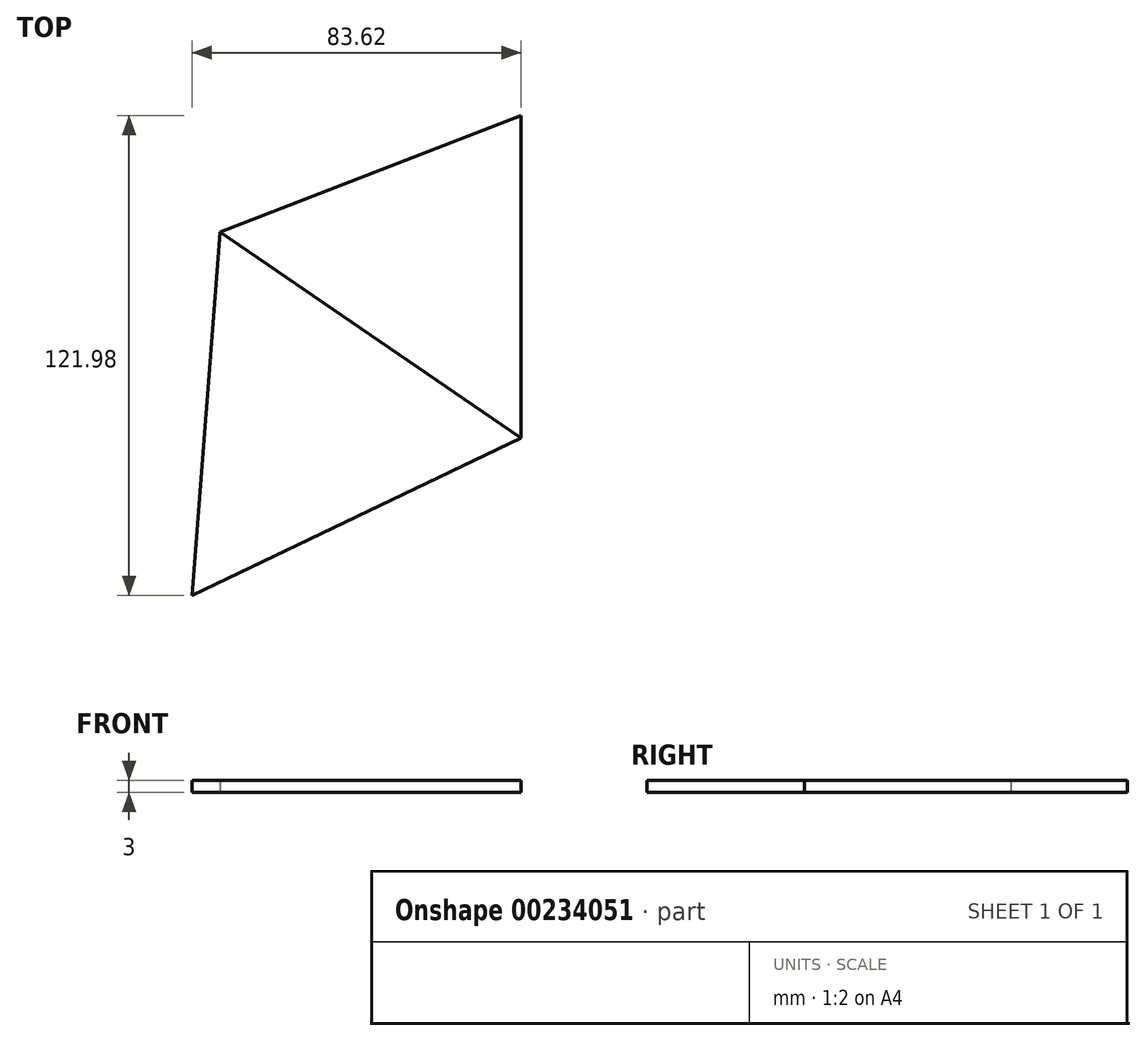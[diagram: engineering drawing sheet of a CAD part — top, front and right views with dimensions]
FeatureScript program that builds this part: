
annotation { "Feature Type Name" : "Feature", "Feature Type Description" : "" }
export const myFeature = defineFeature(function(context is Context, id is Id, definition is map)
    precondition{}
    {
        {
            var Q0;
            Q0=qCreatedBy(makeId("Top.planeOp"),FACE);
            var sketch = newSketch(context, id + "F0", { "sketchPlane" : qUnion([Q0])});
            skLineSegment(sketch, "E0", {"start": v(0, 0) * mm, "end": v(0, -81.97) * mm});
            skLineSegment(sketch, "E1", {"start": v(0, -81.97) * mm, "end": v(-76.46, -29.56) * mm});
            skLineSegment(sketch, "E2", {"start": v(-76.46, -29.56) * mm, "end": v(0, 0) * mm});
            skLineSegment(sketch, "E3", {"start": v(-76.46, -29.56) * mm, "end": v(-83.62, -121.98) * mm});
            skLineSegment(sketch, "E4", {"start": v(-83.62, -121.98) * mm, "end": v(0, -81.97) * mm});
            skLineSegment(sketch, "E5", {"start": v(-76.46, -29.56) * mm, "end": v(-147.45, -70.55) * mm});
            skLineSegment(sketch, "E6", {"start": v(-147.45, -70.55) * mm, "end": v(-83.62, -121.98) * mm});
            skLineSegment(sketch, "E7", {"start": v(-83.62, -121.98) * mm, "end": v(-12.63, -162.97) * mm});
            skLineSegment(sketch, "E8", {"start": v(-12.63, -162.97) * mm, "end": v(0, -81.97) * mm});
            skLineSegment(sketch, "E9", {"start": v(-83.62, -121.98) * mm, "end": v(-172.4, -148.63) * mm});
            skLineSegment(sketch, "E10", {"start": v(-172.4, -148.63) * mm, "end": v(-104.94, -212.2) * mm});
            skLineSegment(sketch, "E11", {"start": v(-104.94, -212.2) * mm, "end": v(-83.62, -121.98) * mm});
            skLineSegment(sketch, "E12", {"start": v(-172.4, -148.63) * mm, "end": v(-147.45, -70.55) * mm});
            skLineSegment(sketch, "E13", {"start": v(-83.62, -121.98) * mm, "end": v(-28.48, -182.64) * mm});
            skLineSegment(sketch, "E14", {"start": v(-28.48, -182.64) * mm, "end": v(-104.94, -212.2) * mm});
            skLineSegment(sketch, "E15", {"start": v(-104.94, -212.2) * mm, "end": v(-28.48, -264.61) * mm});
            skLineSegment(sketch, "E16", {"start": v(-28.48, -264.61) * mm, "end": v(-28.48, -182.64) * mm});
            skLineSegment(sketch, "E17.1.0", {"start": v(-257.08, -68.86) * mm, "end": v(-180.62, -39.3) * mm});
            skLineSegment(sketch, "E17.1.1", {"start": v(-180.62, -39.3) * mm, "end": v(-235.76, 21.36) * mm});
            skLineSegment(sketch, "E17.1.2", {"start": v(-235.76, 21.36) * mm, "end": v(-257.08, -68.86) * mm});
            skLineSegment(sketch, "E17.1.3", {"start": v(-76.46, -29.56) * mm, "end": v(-55.14, 60.66) * mm});
            skLineSegment(sketch, "E17.1.4", {"start": v(-55.14, 60.66) * mm, "end": v(-143.93, 34) * mm});
            skLineSegment(sketch, "E17.1.5", {"start": v(0, 0) * mm, "end": v(-76.46, -29.56) * mm});
            skLineSegment(sketch, "E17.1.6", {"start": v(-143.93, 34) * mm, "end": v(-76.46, -29.56) * mm});
            skLineSegment(sketch, "E17.1.7", {"start": v(-55.14, 60.66) * mm, "end": v(-118.97, 112.1) * mm});
            skLineSegment(sketch, "E17.1.8", {"start": v(-200.8, 107.21) * mm, "end": v(-118.97, 112.1) * mm});
            skLineSegment(sketch, "E17.1.9", {"start": v(-235.76, 21.36) * mm, "end": v(-143.93, 34) * mm});
            skLineSegment(sketch, "E17.1.10", {"start": v(-118.97, 112.1) * mm, "end": v(-143.93, 34) * mm});
            skLineSegment(sketch, "E17.1.11", {"start": v(-143.93, 34) * mm, "end": v(-180.62, -39.3) * mm});
            skLineSegment(sketch, "E17.1.12", {"start": v(-200.8, 107.21) * mm, "end": v(-235.76, 21.36) * mm});
            skLineSegment(sketch, "E17.1.13", {"start": v(-143.93, 34) * mm, "end": v(-156.56, -46.99) * mm});
            skLineSegment(sketch, "E17.1.14", {"start": v(-156.56, -46.99) * mm, "end": v(-76.46, -29.56) * mm});
            skLineSegment(sketch, "E17.1.15", {"start": v(-143.93, 34) * mm, "end": v(-200.8, 107.21) * mm});
            skLineSegment(sketch, "E17.2.0", {"start": v(-156.93, 214.95) * mm, "end": v(-101.79, 154.3) * mm});
            skLineSegment(sketch, "E17.2.1", {"start": v(-101.79, 154.3) * mm, "end": v(-65.1, 227.6) * mm});
            skLineSegment(sketch, "E17.2.2", {"start": v(-65.1, 227.6) * mm, "end": v(-156.93, 214.95) * mm});
            skLineSegment(sketch, "E17.2.3", {"start": v(-55.14, 60.66) * mm, "end": v(36.69, 73.3) * mm});
            skLineSegment(sketch, "E17.2.4", {"start": v(36.69, 73.3) * mm, "end": v(-20.18, 146.51) * mm});
            skLineSegment(sketch, "E17.2.5", {"start": v(0, 0) * mm, "end": v(-55.14, 60.66) * mm});
            skLineSegment(sketch, "E17.2.6", {"start": v(-20.18, 146.51) * mm, "end": v(-55.14, 60.66) * mm});
            skLineSegment(sketch, "E17.2.7", {"start": v(36.69, 73.3) * mm, "end": v(61.65, 151.4) * mm});
            skLineSegment(sketch, "E17.2.8", {"start": v(27.59, 225.95) * mm, "end": v(61.65, 151.4) * mm});
            skLineSegment(sketch, "E17.2.9", {"start": v(-65.1, 227.6) * mm, "end": v(-20.18, 146.51) * mm});
            skLineSegment(sketch, "E17.2.10", {"start": v(61.65, 151.4) * mm, "end": v(-20.18, 146.51) * mm});
            skLineSegment(sketch, "E17.2.11", {"start": v(-20.18, 146.51) * mm, "end": v(-101.79, 154.3) * mm});
            skLineSegment(sketch, "E17.2.12", {"start": v(27.59, 225.95) * mm, "end": v(-65.1, 227.6) * mm});
            skLineSegment(sketch, "E17.2.13", {"start": v(-20.18, 146.51) * mm, "end": v(-100.28, 129.08) * mm});
            skLineSegment(sketch, "E17.2.14", {"start": v(-100.28, 129.08) * mm, "end": v(-55.14, 60.66) * mm});
            skLineSegment(sketch, "E17.2.15", {"start": v(-20.18, 146.51) * mm, "end": v(27.59, 225.95) * mm});
            skLineSegment(sketch, "E17.3.0", {"start": v(143.9, 223.89) * mm, "end": v(107.2, 150.58) * mm});
            skLineSegment(sketch, "E17.3.1", {"start": v(107.2, 150.58) * mm, "end": v(188.81, 142.8) * mm});
            skLineSegment(sketch, "E17.3.2", {"start": v(188.81, 142.8) * mm, "end": v(143.9, 223.89) * mm});
            skLineSegment(sketch, "E17.3.3", {"start": v(36.69, 73.3) * mm, "end": v(81.6, -7.79) * mm});
            skLineSegment(sketch, "E17.3.4", {"start": v(81.6, -7.79) * mm, "end": v(129.37, 71.66) * mm});
            skLineSegment(sketch, "E17.3.5", {"start": v(0, 0) * mm, "end": v(36.69, 73.3) * mm});
            skLineSegment(sketch, "E17.3.6", {"start": v(129.37, 71.66) * mm, "end": v(36.69, 73.3) * mm});
            skLineSegment(sketch, "E17.3.7", {"start": v(81.6, -7.79) * mm, "end": v(163.43, -2.9) * mm});
            skLineSegment(sketch, "E17.3.8", {"start": v(220.7, 55.75) * mm, "end": v(163.43, -2.9) * mm});
            skLineSegment(sketch, "E17.3.9", {"start": v(188.81, 142.8) * mm, "end": v(129.37, 71.66) * mm});
            skLineSegment(sketch, "E17.3.10", {"start": v(163.43, -2.9) * mm, "end": v(129.37, 71.66) * mm});
            skLineSegment(sketch, "E17.3.11", {"start": v(129.37, 71.66) * mm, "end": v(107.2, 150.58) * mm});
            skLineSegment(sketch, "E17.3.12", {"start": v(220.7, 55.75) * mm, "end": v(188.81, 142.8) * mm});
            skLineSegment(sketch, "E17.3.13", {"start": v(129.37, 71.66) * mm, "end": v(84.23, 140.09) * mm});
            skLineSegment(sketch, "E17.3.14", {"start": v(84.23, 140.09) * mm, "end": v(36.69, 73.3) * mm});
            skLineSegment(sketch, "E17.3.15", {"start": v(129.37, 71.66) * mm, "end": v(220.7, 55.75) * mm});
            skLineSegment(sketch, "E17.4.0", {"start": v(260.71, -53.48) * mm, "end": v(179.1, -45.7) * mm});
            skLineSegment(sketch, "E17.4.1", {"start": v(179.1, -45.7) * mm, "end": v(201.27, -124.62) * mm});
            skLineSegment(sketch, "E17.4.2", {"start": v(201.27, -124.62) * mm, "end": v(260.71, -53.48) * mm});
            skLineSegment(sketch, "E17.4.3", {"start": v(81.6, -7.79) * mm, "end": v(22.17, -78.92) * mm});
            skLineSegment(sketch, "E17.4.4", {"start": v(22.17, -78.92) * mm, "end": v(113.5, -94.83) * mm});
            skLineSegment(sketch, "E17.4.5", {"start": v(0, 0) * mm, "end": v(81.6, -7.79) * mm});
            skLineSegment(sketch, "E17.4.6", {"start": v(113.5, -94.83) * mm, "end": v(81.6, -7.79) * mm});
            skLineSegment(sketch, "E17.4.7", {"start": v(22.17, -78.92) * mm, "end": v(56.23, -153.49) * mm});
            skLineSegment(sketch, "E17.4.8", {"start": v(131.59, -185.75) * mm, "end": v(56.23, -153.49) * mm});
            skLineSegment(sketch, "E17.4.9", {"start": v(201.27, -124.62) * mm, "end": v(113.5, -94.83) * mm});
            skLineSegment(sketch, "E17.4.10", {"start": v(56.23, -153.49) * mm, "end": v(113.5, -94.83) * mm});
            skLineSegment(sketch, "E17.4.11", {"start": v(113.5, -94.83) * mm, "end": v(179.1, -45.7) * mm});
            skLineSegment(sketch, "E17.4.12", {"start": v(131.59, -185.75) * mm, "end": v(201.27, -124.62) * mm});
            skLineSegment(sketch, "E17.4.13", {"start": v(113.5, -94.83) * mm, "end": v(161.04, -28.05) * mm});
            skLineSegment(sketch, "E17.4.14", {"start": v(161.04, -28.05) * mm, "end": v(81.6, -7.79) * mm});
            skLineSegment(sketch, "E17.4.15", {"start": v(113.5, -94.83) * mm, "end": v(131.59, -185.75) * mm});
            skPoint(sketch, "E17.center", {"position": v(0, 0) * mm});
            skLineSegment(sketch, "E17.anchor1", {"start": v(0, 0) * mm, "end": v(-172.4, -148.63) * mm, "construction": true});
            skLineSegment(sketch, "E17.anchor2", {"start": v(0, 0) * mm, "end": v(131.59, -185.75) * mm, "construction": true});
            skLineSegment(sketch, "E18", {"start": v(0, 0) * mm, "end": v(22.17, -78.92) * mm});
            skLineSegment(sketch, "E19.MirrorCS", {"start": v(-456.15, 107.78) * mm, "end": v(-401.01, 47.12) * mm});
            skLineSegment(sketch, "E20.MirrorCS", {"start": v(-379.7, 322.18) * mm, "end": v(-296.07, 282.17) * mm});
            skLineSegment(sketch, "E21.MirrorCS", {"start": v(-401.01, 47.12) * mm, "end": v(-456.15, 107.78) * mm});
            skLineSegment(sketch, "E22.MirrorCS", {"start": v(-456.15, 107.78) * mm, "end": v(-511.3, 47.12) * mm});
            skLineSegment(sketch, "E23.MirrorCS", {"start": v(-456.15, 107.78) * mm, "end": v(-492.84, 34.47) * mm});
            skLineSegment(sketch, "E24.MirrorCS", {"start": v(-492.84, 34.47) * mm, "end": v(-401.01, 47.12) * mm});
            skLineSegment(sketch, "E25.MirrorCS", {"start": v(-401.01, 47.12) * mm, "end": v(-355.87, -21.3) * mm});
            skLineSegment(sketch, "E26.MirrorCS", {"start": v(-401.01, 47.12) * mm, "end": v(-435.97, -38.73) * mm});
            skLineSegment(sketch, "E27.MirrorCS", {"start": v(-435.97, -38.73) * mm, "end": v(-492.84, 34.47) * mm});
            skLineSegment(sketch, "E28.MirrorCS", {"start": v(-435.97, -38.73) * mm, "end": v(-517.8, -43.61) * mm});
            skLineSegment(sketch, "E29.MirrorCS", {"start": v(-435.97, -38.73) * mm, "end": v(-368.5, -102.3) * mm});
            skLineSegment(sketch, "E30.MirrorCS", {"start": v(-435.97, -38.73) * mm, "end": v(-512.43, -68.3) * mm});
            skLineSegment(sketch, "E31.MirrorCS", {"start": v(-457.29, -128.95) * mm, "end": v(-435.97, -38.73) * mm});
            skLineSegment(sketch, "E32.MirrorCS", {"start": v(-512.43, -68.3) * mm, "end": v(-457.29, -128.95) * mm});
            skLineSegment(sketch, "E33.MirrorCS", {"start": v(-296.07, 282.17) * mm, "end": v(-219.61, 229.76) * mm});
            skLineSegment(sketch, "E34.MirrorCS", {"start": v(-561.1, 319.98) * mm, "end": v(-484.63, 372.4) * mm});
            skLineSegment(sketch, "E35.MirrorCS", {"start": v(-484.63, 372.4) * mm, "end": v(-484.63, 290.42) * mm});
            skLineSegment(sketch, "E36.MirrorCS", {"start": v(-379.7, 322.18) * mm, "end": v(-443.53, 270.75) * mm});
            skLineSegment(sketch, "E37.MirrorCS", {"start": v(-372.53, 229.76) * mm, "end": v(-379.7, 322.18) * mm});
            skLineSegment(sketch, "E38.MirrorCS", {"start": v(-296.07, 282.17) * mm, "end": v(-372.53, 229.76) * mm});
            skLineSegment(sketch, "E39.MirrorCS", {"start": v(-296.07, 200.2) * mm, "end": v(-296.07, 282.17) * mm});
            skLineSegment(sketch, "E40.MirrorCS", {"start": v(-219.61, 229.76) * mm, "end": v(-296.07, 200.2) * mm});
            skLineSegment(sketch, "E41.MirrorCS", {"start": v(-484.63, 290.42) * mm, "end": v(-561.1, 319.98) * mm});
            skLineSegment(sketch, "E42.MirrorCS", {"start": v(-443.53, 270.75) * mm, "end": v(-372.53, 229.76) * mm});
            skLineSegment(sketch, "E43.MirrorCS", {"start": v(-372.53, 229.76) * mm, "end": v(-296.07, 200.2) * mm});
            skLineSegment(sketch, "E44.MirrorCS", {"start": v(-372.53, 229.76) * mm, "end": v(-308.7, 178.33) * mm});
            skLineSegment(sketch, "E45.MirrorCS", {"start": v(-561.1, 319.98) * mm, "end": v(-539.78, 229.76) * mm});
            skLineSegment(sketch, "E46.MirrorCS", {"start": v(-539.78, 229.76) * mm, "end": v(-484.63, 290.42) * mm});
            skLineSegment(sketch, "E47.MirrorCS", {"start": v(-539.78, 229.76) * mm, "end": v(-468.78, 270.75) * mm});
            skLineSegment(sketch, "E48.MirrorCS", {"start": v(-468.78, 270.75) * mm, "end": v(-456.15, 189.75) * mm});
            skLineSegment(sketch, "E49.MirrorCS", {"start": v(-456.15, 189.75) * mm, "end": v(-443.53, 270.75) * mm});
            skLineSegment(sketch, "E50.MirrorCS", {"start": v(-628.56, 256.4) * mm, "end": v(-561.1, 319.98) * mm});
            skLineSegment(sketch, "E51.MirrorCS", {"start": v(-456.15, 189.75) * mm, "end": v(-372.53, 229.76) * mm});
            skLineSegment(sketch, "E52.MirrorCS", {"start": v(-228.6, 113.78) * mm, "end": v(-299.6, 154.77) * mm});
            skLineSegment(sketch, "E53.MirrorCS", {"start": v(-372.53, 229.76) * mm, "end": v(-379.7, 137.34) * mm});
            skLineSegment(sketch, "E54.MirrorCS", {"start": v(-308.7, 178.33) * mm, "end": v(-379.7, 137.34) * mm});
            skLineSegment(sketch, "E55.MirrorCS", {"start": v(-539.78, 229.76) * mm, "end": v(-456.15, 189.75) * mm});
            skLineSegment(sketch, "E56.MirrorCS", {"start": v(-539.78, 229.76) * mm, "end": v(-628.56, 256.4) * mm});
            skLineSegment(sketch, "E57.MirrorCS", {"start": v(-379.7, 137.34) * mm, "end": v(-299.6, 154.77) * mm});
            skLineSegment(sketch, "E58.MirrorCS", {"start": v(-379.7, 137.34) * mm, "end": v(-456.15, 189.75) * mm});
            skLineSegment(sketch, "E59.MirrorCS", {"start": v(-299.6, 154.77) * mm, "end": v(-312.22, 73.77) * mm});
            skLineSegment(sketch, "E60.MirrorCS", {"start": v(-312.22, 73.77) * mm, "end": v(-228.6, 113.78) * mm});
            skLineSegment(sketch, "E61.MirrorCS", {"start": v(-603.6, 178.33) * mm, "end": v(-539.78, 229.76) * mm});
            skLineSegment(sketch, "E62.MirrorCS", {"start": v(-456.15, 107.78) * mm, "end": v(-456.15, 189.75) * mm});
            skLineSegment(sketch, "E63.MirrorCS", {"start": v(-379.7, 137.34) * mm, "end": v(-312.22, 73.77) * mm});
            skLineSegment(sketch, "E64.MirrorCS", {"start": v(-228.6, 113.78) * mm, "end": v(-235.76, 21.36) * mm});
            skLineSegment(sketch, "E65.MirrorCS", {"start": v(-628.56, 256.4) * mm, "end": v(-603.6, 178.33) * mm});
            skLineSegment(sketch, "E66.MirrorCS", {"start": v(-532.61, 137.34) * mm, "end": v(-539.78, 229.76) * mm});
            skLineSegment(sketch, "E67.MirrorCS", {"start": v(-456.15, 189.75) * mm, "end": v(-532.61, 137.34) * mm});
            skLineSegment(sketch, "E68.MirrorCS", {"start": v(-456.15, 107.78) * mm, "end": v(-379.7, 137.34) * mm});
            skLineSegment(sketch, "E69.MirrorCS", {"start": v(-235.76, 21.36) * mm, "end": v(-312.22, 73.77) * mm});
            skLineSegment(sketch, "E70.MirrorCS", {"start": v(-532.61, 137.34) * mm, "end": v(-603.6, 178.33) * mm});
            skLineSegment(sketch, "E71.MirrorCS", {"start": v(-456.15, 107.78) * mm, "end": v(-532.61, 137.34) * mm});
            skPoint(sketch, "E72.MirrorP", {"position": v(-456.15, 107.78) * mm});
            skLineSegment(sketch, "E73.MirrorCS", {"start": v(-401.01, 47.12) * mm, "end": v(-379.7, 137.34) * mm});
            skLineSegment(sketch, "E74.MirrorCS", {"start": v(-612.71, 154.77) * mm, "end": v(-532.61, 137.34) * mm});
            skLineSegment(sketch, "E75.MirrorCS", {"start": v(-312.22, 73.77) * mm, "end": v(-401.01, 47.12) * mm});
            skLineSegment(sketch, "E76.MirrorCS", {"start": v(-312.22, 73.77) * mm, "end": v(-312.22, -8.2) * mm});
            skLineSegment(sketch, "E77.MirrorCS", {"start": v(-312.22, 73.77) * mm, "end": v(-337.18, -4.31) * mm});
            skLineSegment(sketch, "E78.MirrorCS", {"start": v(-312.22, -8.2) * mm, "end": v(-235.76, 21.36) * mm});
            skLineSegment(sketch, "E79.MirrorCS", {"start": v(-713.23, 176.64) * mm, "end": v(-636.77, 147.08) * mm});
            skLineSegment(sketch, "E80.MirrorCS", {"start": v(-337.18, -4.31) * mm, "end": v(-401.01, 47.12) * mm});
            skLineSegment(sketch, "E81.MirrorCS", {"start": v(-532.61, 137.34) * mm, "end": v(-511.3, 47.12) * mm});
            skLineSegment(sketch, "E82.MirrorCS", {"start": v(-600.09, 73.77) * mm, "end": v(-612.71, 154.77) * mm});
            skLineSegment(sketch, "E83.MirrorCS", {"start": v(-600.09, 73.77) * mm, "end": v(-532.61, 137.34) * mm});
            skLineSegment(sketch, "E84.MirrorCS", {"start": v(-600.09, 73.77) * mm, "end": v(-636.77, 147.08) * mm});
            skLineSegment(sketch, "E85.MirrorCS", {"start": v(-257.08, -68.86) * mm, "end": v(-312.22, -8.2) * mm});
            skLineSegment(sketch, "E86.MirrorCS", {"start": v(-691.92, 86.42) * mm, "end": v(-713.23, 176.64) * mm});
            skLineSegment(sketch, "E87.MirrorCS", {"start": v(-636.77, 147.08) * mm, "end": v(-691.92, 86.42) * mm});
            skLineSegment(sketch, "E88.MirrorCS", {"start": v(-511.3, 47.12) * mm, "end": v(-600.09, 73.77) * mm});
            skLineSegment(sketch, "E89.MirrorCS", {"start": v(-517.8, -43.61) * mm, "end": v(-492.84, 34.47) * mm});
            skLineSegment(sketch, "E90.MirrorCS", {"start": v(-691.92, 86.42) * mm, "end": v(-600.09, 73.77) * mm});
            skLineSegment(sketch, "E91.MirrorCS", {"start": v(-355.87, -21.3) * mm, "end": v(-435.97, -38.73) * mm});
            skLineSegment(sketch, "E92.MirrorCS", {"start": v(-511.3, 47.12) * mm, "end": v(-575.13, -4.31) * mm});
            skLineSegment(sketch, "E93.MirrorCS", {"start": v(-456.15, 107.78) * mm, "end": v(-368.5, -102.3) * mm, "construction": true});
            skLineSegment(sketch, "E94.MirrorCS", {"start": v(-368.5, -102.3) * mm, "end": v(-355.87, -21.3) * mm});
            skLineSegment(sketch, "E95.MirrorCS", {"start": v(-575.13, -4.31) * mm, "end": v(-600.09, 73.77) * mm});
            skLineSegment(sketch, "E96.MirrorCS", {"start": v(-600.09, 73.77) * mm, "end": v(-656.96, 0.57) * mm});
            skLineSegment(sketch, "E97.MirrorCS", {"start": v(-656.96, 0.57) * mm, "end": v(-691.92, 86.42) * mm});
            skLineSegment(sketch, "E98.MirrorCS", {"start": v(-456.15, 107.78) * mm, "end": v(-656.96, 0.57) * mm, "construction": true});
            skLineSegment(sketch, "E99.MirrorCS", {"start": v(-656.96, 0.57) * mm, "end": v(-575.13, -4.31) * mm});
            skLineSegment(sketch, "E100.MirrorCS", {"start": v(-368.5, -102.3) * mm, "end": v(-457.29, -128.95) * mm});
            skLineSegment(sketch, "E101.MirrorCS", {"start": v(-549.12, -141.6) * mm, "end": v(-512.43, -68.3) * mm});
            skLineSegment(sketch, "E102.MirrorCS", {"start": v(-457.29, -128.95) * mm, "end": v(-549.12, -141.6) * mm});
            skSolve(sketch);
        }
        {
            var Q0;
            Q0=makeQuery(id+"F0.imprint","IMPRINT",FACE,{"disambiguationData":[TD([[makeQuery(id+"F0.imprint","IMPRINT",EDGE,{"derivedFrom":sQuery(id+"F0.wireOp",EDGE,"E0")}),-1.0]])]});
            extrude(context, id + "F1", {"entities" : qUnion([Q0]), "depth" : 3 * mm});
        }
        {
            var Q0;
            Q0=makeQuery(id+"F0.imprint","IMPRINT",FACE,{"disambiguationData":[TD([[makeQuery(id+"F0.imprint","IMPRINT",EDGE,{"derivedFrom":sQuery(id+"F0.wireOp",EDGE,"E1")}),1.0]])]});
            extrude(context, id + "F2", {"entities" : qUnion([Q0]), "depth" : 3 * mm});
        }
    });
